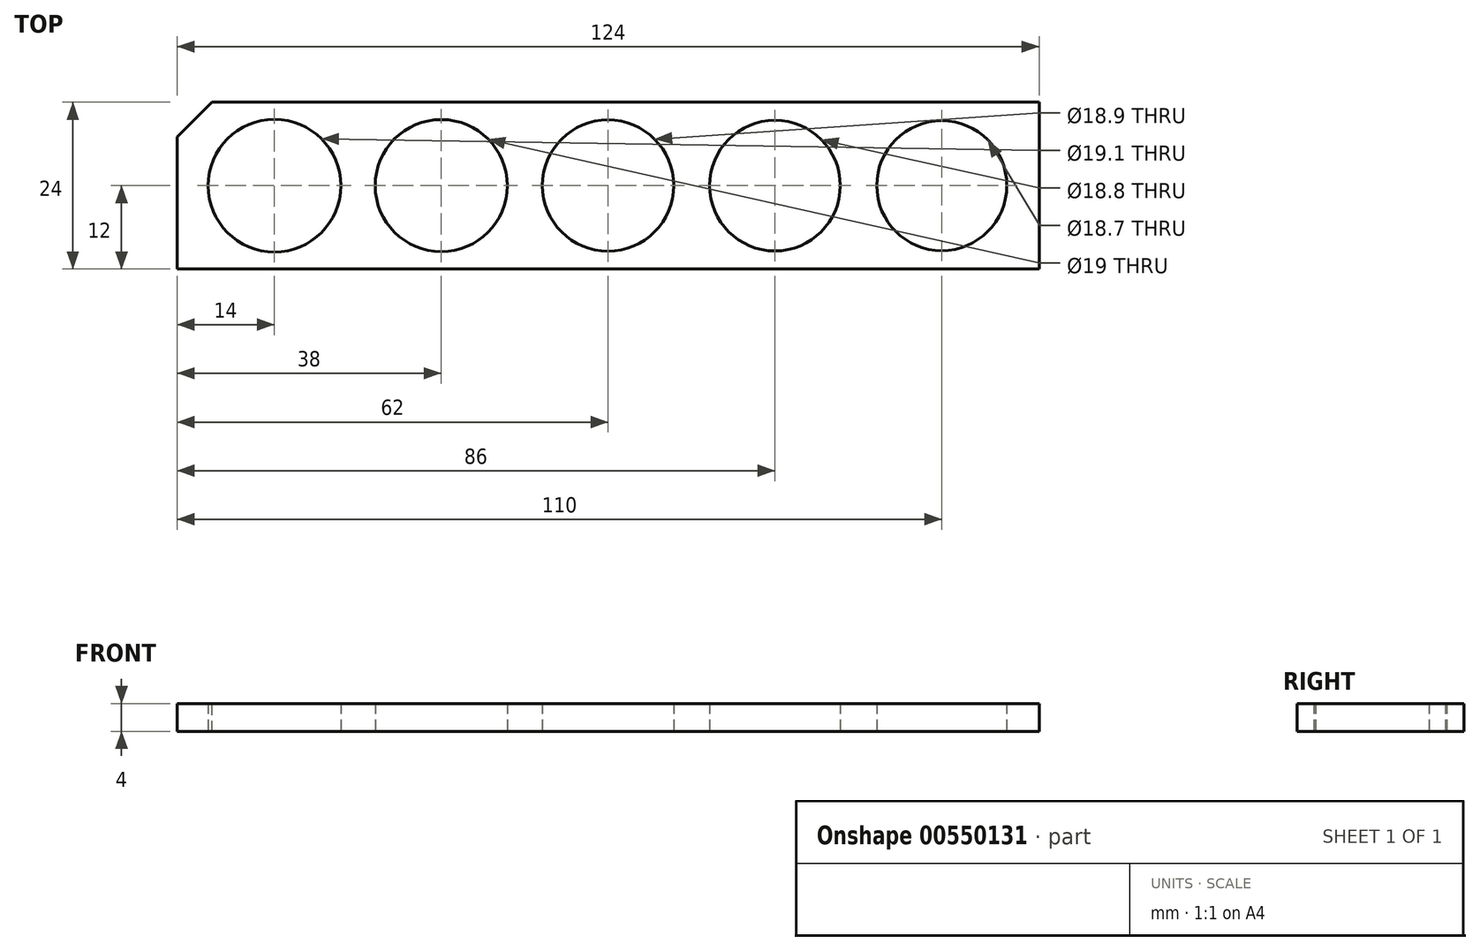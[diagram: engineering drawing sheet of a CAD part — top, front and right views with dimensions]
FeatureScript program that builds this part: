
annotation { "Feature Type Name" : "Feature", "Feature Type Description" : "" }
export const myFeature = defineFeature(function(context is Context, id is Id, definition is map)
    precondition{}
    {
        {
            var Q0;
            Q0=qCreatedBy(makeId("Top.planeOp"),FACE);
            var sketch = newSketch(context, id + "F0", { "sketchPlane" : qUnion([Q0])});
            skLineSegment(sketch, "E0", {"start": v(0, 0) * mm, "end": v(-24, 0) * mm});
            skCircle(sketch, "E1", {"center": v(-24, 0) * mm, "radius": 9.5 * mm});
            skLineSegment(sketch, "E2", {"start": v(-24, 0) * mm, "end": v(-48, 0) * mm});
            skCircle(sketch, "E3", {"center": v(-48, 0) * mm, "radius": 9.55 * mm});
            skLineSegment(sketch, "E4", {"start": v(0, 0) * mm, "end": v(24, 0) * mm});
            skLineSegment(sketch, "E5", {"start": v(24, 0) * mm, "end": v(48, 0) * mm});
            skCircle(sketch, "E6", {"center": v(0, 0) * mm, "radius": 9.45 * mm});
            skCircle(sketch, "E7", {"center": v(24, 0) * mm, "radius": 9.4 * mm});
            skCircle(sketch, "E8", {"center": v(48, 0) * mm, "radius": 9.35 * mm});
            skLineSegment(sketch, "E9.bottom", {"start": v(62, -12) * mm, "end": v(-62, -12) * mm});
            skLineSegment(sketch, "E9.top", {"start": v(62, 12) * mm, "end": v(-62, 12) * mm});
            skLineSegment(sketch, "E9.left", {"start": v(62, -12) * mm, "end": v(62, 12) * mm});
            skLineSegment(sketch, "E9.right", {"start": v(-62, -12) * mm, "end": v(-62, 12) * mm});
            skSolve(sketch);
        }
        {
            var Q0;
            Q0 = qSketchRegion(id + "F0", true);
            extrude(context, id + "F1", {"entities" : qUnion([Q0]), "depth" : 4 * mm, "offsetDistance" : 25 * mm});
        }
        {
            var Q0;
            Q0=makeQuery(id+"F1.opExtrude","SWEPT_EDGE",EDGE,{"disambiguationData":[OSD([sQuery(id+"F0.wireOp",EDGE,"E9.top"),sQuery(id+"F0.wireOp",EDGE,"E9.right")])]});
            chamfer(context, id + "F2", {"entities" : qUnion([Q0]), "width" : 5 * mm, "tangentPropagation" : true});
        }
    });
